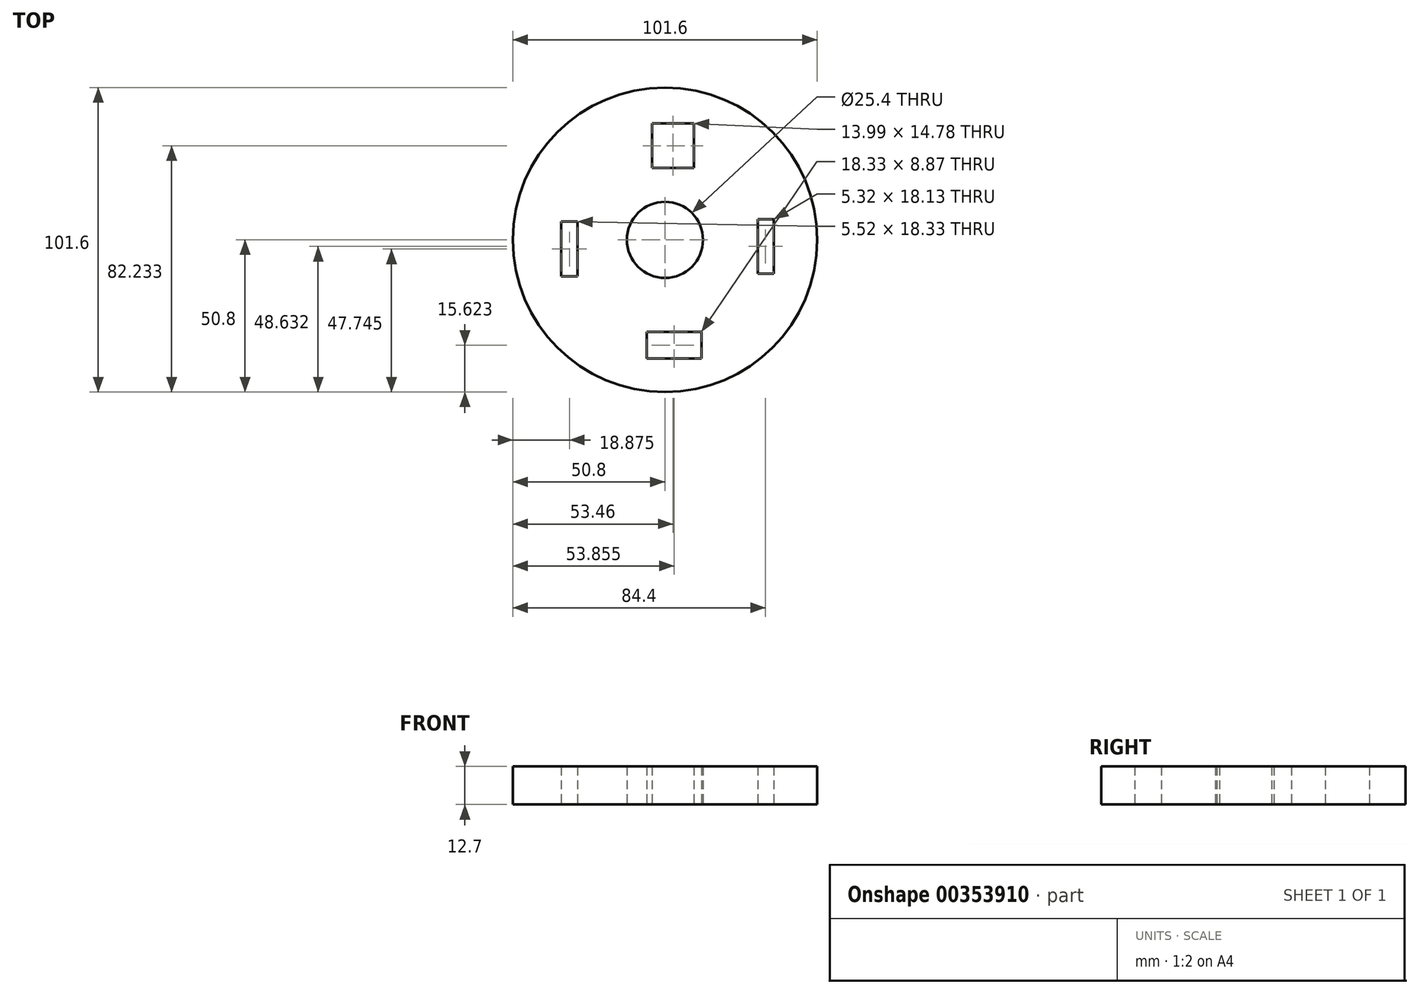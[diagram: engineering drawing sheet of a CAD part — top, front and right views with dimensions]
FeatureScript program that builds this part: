
annotation { "Feature Type Name" : "Feature", "Feature Type Description" : "" }
export const myFeature = defineFeature(function(context is Context, id is Id, definition is map)
    precondition{}
    {
        {
            var Q0;
            Q0=qCreatedBy(makeId("Top.planeOp"),FACE);
            var sketch = newSketch(context, id + "F0", { "sketchPlane" : qUnion([Q0])});
            skCircle(sketch, "E0", {"center": v(0, 0) * mm, "radius": 50.8 * mm});
            skCircle(sketch, "E1", {"center": v(0, 0) * mm, "radius": 12.7 * mm});
            skLineSegment(sketch, "E2.bottom", {"start": v(-4.34, 38.82) * mm, "end": v(9.66, 38.82) * mm});
            skLineSegment(sketch, "E2.top", {"start": v(-4.34, 24.04) * mm, "end": v(9.66, 24.04) * mm});
            skLineSegment(sketch, "E2.left", {"start": v(-4.34, 38.82) * mm, "end": v(-4.34, 24.04) * mm});
            skLineSegment(sketch, "E2.right", {"start": v(9.66, 38.82) * mm, "end": v(9.66, 24.04) * mm});
            skLineSegment(sketch, "E3.bottom", {"start": v(-6.1, -30.74) * mm, "end": v(12.22, -30.74) * mm});
            skLineSegment(sketch, "E3.top", {"start": v(-6.1, -39.61) * mm, "end": v(12.22, -39.61) * mm});
            skLineSegment(sketch, "E3.left", {"start": v(-6.1, -30.74) * mm, "end": v(-6.1, -39.61) * mm});
            skLineSegment(sketch, "E3.right", {"start": v(12.22, -30.74) * mm, "end": v(12.22, -39.61) * mm});
            skLineSegment(sketch, "E4.bottom", {"start": v(30.94, 6.9) * mm, "end": v(36.26, 6.9) * mm});
            skLineSegment(sketch, "E4.top", {"start": v(30.94, -11.23) * mm, "end": v(36.26, -11.23) * mm});
            skLineSegment(sketch, "E4.left", {"start": v(30.94, 6.9) * mm, "end": v(30.94, -11.23) * mm});
            skLineSegment(sketch, "E4.right", {"start": v(36.26, 6.9) * mm, "end": v(36.26, -11.23) * mm});
            skLineSegment(sketch, "E5.bottom", {"start": v(-34.68, 6.1) * mm, "end": v(-29.17, 6.1) * mm});
            skLineSegment(sketch, "E5.top", {"start": v(-34.68, -12.22) * mm, "end": v(-29.17, -12.22) * mm});
            skLineSegment(sketch, "E5.left", {"start": v(-34.68, 6.1) * mm, "end": v(-34.68, -12.22) * mm});
            skLineSegment(sketch, "E5.right", {"start": v(-29.17, 6.1) * mm, "end": v(-29.17, -12.22) * mm});
            skSolve(sketch);
        }
        {
            var Q0;
            Q0=makeQuery(id+"F0.imprint","IMPRINT",FACE,{"disambiguationData":[TD([[makeQuery(id+"F0.imprint","IMPRINT",EDGE,{"derivedFrom":sQuery(id+"F0.wireOp",EDGE,"E0")}),1.0]])]});
            extrude(context, id + "F1", {"entities" : qUnion([Q0]), "depth" : 12.7 * mm});
        }
    });
